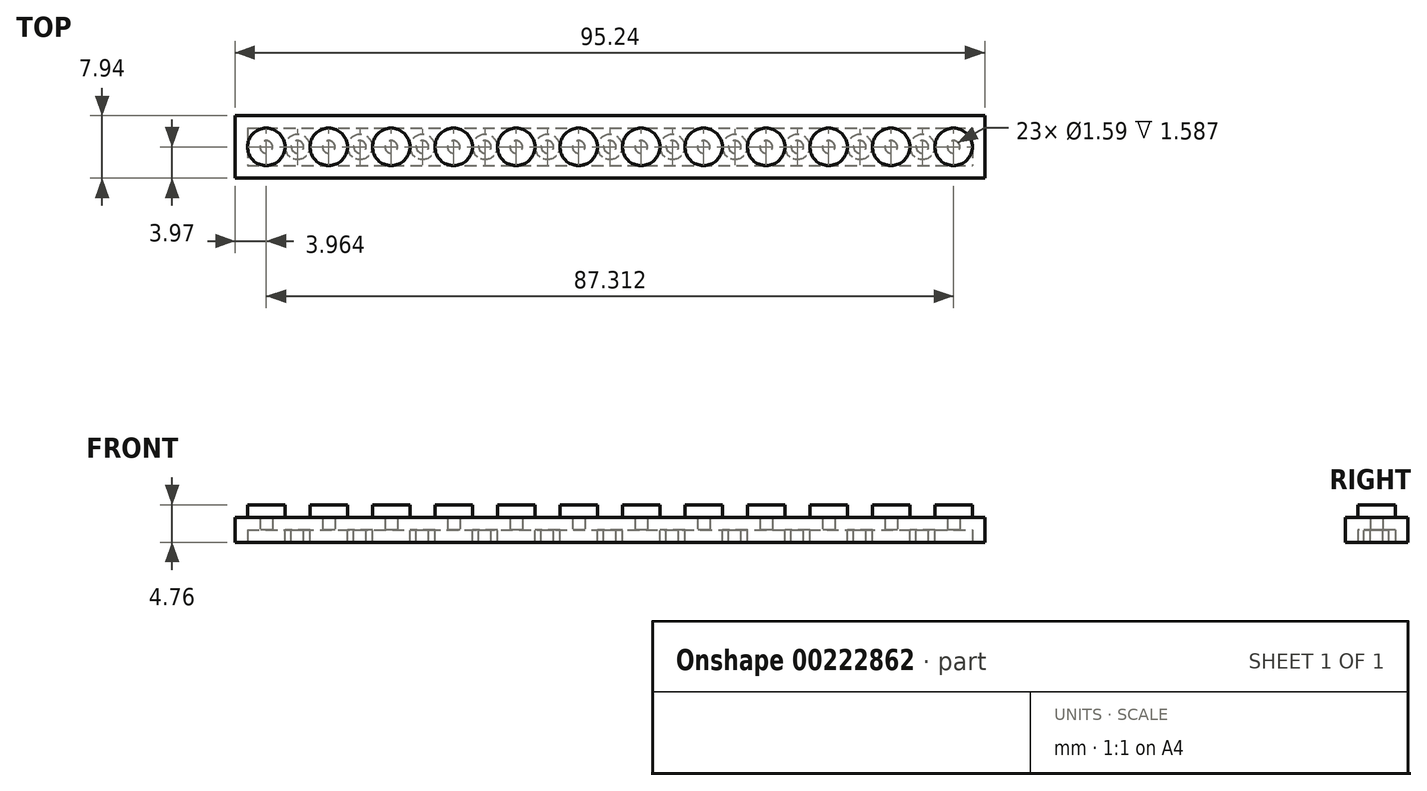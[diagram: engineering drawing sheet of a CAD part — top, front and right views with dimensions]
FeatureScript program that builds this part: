
annotation { "Feature Type Name" : "Feature", "Feature Type Description" : "" }
export const myFeature = defineFeature(function(context is Context, id is Id, definition is map)
    precondition{}
    {
        {
            var Q0;
            Q0=qCreatedBy(makeId("Top.planeOp"),FACE);
            var sketch = newSketch(context, id + "F0", { "sketchPlane" : qUnion([Q0])});
            skLineSegment(sketch, "E0.bottom", {"start": v(-47.63, 3.97) * mm, "end": v(47.62, 3.97) * mm});
            skLineSegment(sketch, "E0.top", {"start": v(-47.63, -3.97) * mm, "end": v(47.62, -3.97) * mm});
            skLineSegment(sketch, "E0.left", {"start": v(-47.63, 3.97) * mm, "end": v(-47.63, -3.97) * mm});
            skLineSegment(sketch, "E0.right", {"start": v(47.62, 3.97) * mm, "end": v(47.62, -3.97) * mm});
            skPoint(sketch, "E0.middle", {"position": v(0, 0) * mm});
            skCircle(sketch, "E1", {"center": v(-43.66, 0) * mm, "radius": 2.38 * mm});
            skCircle(sketch, "E2.1.0.0", {"center": v(-35.72, 0) * mm, "radius": 2.38 * mm});
            skCircle(sketch, "E2.2.0.0", {"center": v(-27.78, 0) * mm, "radius": 2.38 * mm});
            skLineSegment(sketch, "E2.direction1", {"start": v(-43.66, 0) * mm, "end": v(-35.72, 0) * mm, "construction": true});
            skCircle(sketch, "E3.0.3.0", {"center": v(-19.84, 0) * mm, "radius": 2.38 * mm});
            skCircle(sketch, "E4.0.4.0", {"center": v(-11.9, 0) * mm, "radius": 2.38 * mm});
            skCircle(sketch, "E4.0.5.0", {"center": v(-3.97, 0) * mm, "radius": 2.38 * mm});
            skCircle(sketch, "E4.0.6.0", {"center": v(3.97, 0) * mm, "radius": 2.38 * mm});
            skCircle(sketch, "E4.0.7.0", {"center": v(11.9, 0) * mm, "radius": 2.38 * mm});
            skCircle(sketch, "E5.0.8.0", {"center": v(19.84, 0) * mm, "radius": 2.38 * mm});
            skCircle(sketch, "E5.0.9.0", {"center": v(27.78, 0) * mm, "radius": 2.38 * mm});
            skCircle(sketch, "E5.0.10.0", {"center": v(35.72, 0) * mm, "radius": 2.38 * mm});
            skCircle(sketch, "E5.0.11.0", {"center": v(43.66, 0) * mm, "radius": 2.38 * mm});
            skSolve(sketch);
        }
        {
            var Q0;
            Q0=makeQuery(id+"F0.imprint","IMPRINT",FACE,{"disambiguationData":[TD([[makeQuery(id+"F0.imprint","IMPRINT",EDGE,{"derivedFrom":sQuery(id+"F0.wireOp",EDGE,"E0.bottom")}),-1.0]])]});
            extrude(context, id + "F1", {"entities" : qUnion([Q0]), "depth" : 3.17 * mm});
        }
        {
            var Q0;
            Q0=makeQuery(id+"F0.imprint","IMPRINT",FACE,{"disambiguationData":[TD([[makeQuery(id+"F0.imprint","IMPRINT",EDGE,{"derivedFrom":sQuery(id+"F0.wireOp",EDGE,"8b71ed98-f0e1-4300-85cb-82ad82c44b3e0.MirrorC")}),-1.0]])]});
            var Q1;
            Q1=makeQuery(id+"F0.imprint","IMPRINT",FACE,{"disambiguationData":[TD([[makeQuery(id+"F0.imprint","IMPRINT",EDGE,{"derivedFrom":sQuery(id+"F0.wireOp",EDGE,"E1")}),1.0]])]});
            var Q2;
            Q2=makeQuery(id+"F0.imprint","IMPRINT",FACE,{"disambiguationData":[TD([[makeQuery(id+"F0.imprint","IMPRINT",EDGE,{"derivedFrom":sQuery(id+"F0.wireOp",EDGE,"E2.2.0.0")}),1.0]])]});
            var Q3;
            Q3=makeQuery(id+"F0.imprint","IMPRINT",FACE,{"disambiguationData":[TD([[makeQuery(id+"F0.imprint","IMPRINT",EDGE,{"derivedFrom":sQuery(id+"F0.wireOp",EDGE,"E2.1.0.0")}),1.0]])]});
            var Q4;
            Q4=makeQuery(id+"F0.imprint","IMPRINT",FACE,{"disambiguationData":[TD([[makeQuery(id+"F0.imprint","IMPRINT",EDGE,{"derivedFrom":sQuery(id+"F0.wireOp",EDGE,"E3.0.3.0")}),1.0]])]});
            var Q5;
            Q5=makeQuery(id+"F0.imprint","IMPRINT",FACE,{"disambiguationData":[TD([[makeQuery(id+"F0.imprint","IMPRINT",EDGE,{"derivedFrom":sQuery(id+"F0.wireOp",EDGE,"E4.0.4.0")}),1.0]])]});
            var Q6;
            Q6=makeQuery(id+"F0.imprint","IMPRINT",FACE,{"disambiguationData":[TD([[makeQuery(id+"F0.imprint","IMPRINT",EDGE,{"derivedFrom":sQuery(id+"F0.wireOp",EDGE,"E4.0.5.0")}),1.0]])]});
            var Q7;
            Q7=makeQuery(id+"F0.imprint","IMPRINT",FACE,{"disambiguationData":[TD([[makeQuery(id+"F0.imprint","IMPRINT",EDGE,{"derivedFrom":sQuery(id+"F0.wireOp",EDGE,"E4.0.6.0")}),1.0]])]});
            var Q8;
            Q8=makeQuery(id+"F0.imprint","IMPRINT",FACE,{"disambiguationData":[TD([[makeQuery(id+"F0.imprint","IMPRINT",EDGE,{"derivedFrom":sQuery(id+"F0.wireOp",EDGE,"E4.0.7.0")}),1.0]])]});
            var Q9;
            Q9=makeQuery(id+"F0.imprint","IMPRINT",FACE,{"disambiguationData":[TD([[makeQuery(id+"F0.imprint","IMPRINT",EDGE,{"derivedFrom":sQuery(id+"F0.wireOp",EDGE,"E5.0.8.0")}),1.0]])]});
            var Q10;
            Q10=makeQuery(id+"F0.imprint","IMPRINT",FACE,{"disambiguationData":[TD([[makeQuery(id+"F0.imprint","IMPRINT",EDGE,{"derivedFrom":sQuery(id+"F0.wireOp",EDGE,"E5.0.9.0")}),1.0]])]});
            var Q11;
            Q11=makeQuery(id+"F0.imprint","IMPRINT",FACE,{"disambiguationData":[TD([[makeQuery(id+"F0.imprint","IMPRINT",EDGE,{"derivedFrom":sQuery(id+"F0.wireOp",EDGE,"E5.0.10.0")}),1.0]])]});
            var Q12;
            Q12=makeQuery(id+"F0.imprint","IMPRINT",FACE,{"disambiguationData":[TD([[makeQuery(id+"F0.imprint","IMPRINT",EDGE,{"derivedFrom":sQuery(id+"F0.wireOp",EDGE,"E5.0.11.0")}),1.0]])]});
            extrude(context, id + "F2", {"entities" : qUnion([Q0, Q1, Q2, Q3, Q4, Q5, Q6, Q7, Q8, Q9, Q10, Q11, Q12]), "operationType" : NewBodyOperationType.ADD, "depth" : 4.76 * mm});
        }
        {
            var Q0;
            {var subQ0=sQuery(id+"F0.wireOp",EDGE,"8b71ed98-f0e1-4300-85cb-82ad82c44b3e0.MirrorC");var subQ1=sQuery(id+"F0.wireOp",EDGE,"E1");Q0=makeQuery(id+"F2.boolean.opBoolean","MERGE",FACE,{"derivedFrom":[makeQuery(id+"F1.opExtrude","CAP_FACE",FACE,{"disambiguationData":[OSD([sQuery(id+"F0.wireOp",EDGE,"E0.bottom"),sQuery(id+"F0.wireOp",EDGE,"E0.top"),sQuery(id+"F0.wireOp",EDGE,"E0.left"),sQuery(id+"F0.wireOp",EDGE,"E0.right"),subQ1,subQ0])],"isStart":true}),makeQuery(id+"F2.opExtrude","CAP_FACE",FACE,{"disambiguationData":[OSD([subQ1])],"isStart":true}),makeQuery(id+"F2.opExtrude","CAP_FACE",FACE,{"disambiguationData":[OSD([subQ0])],"isStart":true})]});}
            shell(context, id + "F3", {"entities" : qUnion([Q0]), "thickness" : 1.59 * mm});
        }
        {
            var Q0;
            Q0=makeQuery(id+"F3.opShell","OFFSET_FACE",FACE,{"disambiguationData":[OSD([sQuery(id+"F0.wireOp",EDGE,"E0.bottom"),sQuery(id+"F0.wireOp",EDGE,"E0.top"),sQuery(id+"F0.wireOp",EDGE,"E0.left"),sQuery(id+"F0.wireOp",EDGE,"E0.right"),sQuery(id+"F0.wireOp",EDGE,"E1"),sQuery(id+"F0.wireOp",EDGE,"8b71ed98-f0e1-4300-85cb-82ad82c44b3e0.MirrorC")])]});
            var sketch = newSketch(context, id + "F4", { "sketchPlane" : qUnion([Q0])});
            skCircle(sketch, "E6.1.0.0", {"center": v(-39.69, 0) * mm, "radius": 1.59 * mm});
            skCircle(sketch, "E6.1.0.1", {"center": v(-39.69, 0) * mm, "radius": 0.8 * mm});
            skCircle(sketch, "E7.1.0.0", {"center": v(-31.75, 0) * mm, "radius": 1.59 * mm});
            skCircle(sketch, "E7.1.0.1", {"center": v(-31.75, 0) * mm, "radius": 0.8 * mm});
            skCircle(sketch, "E7.2.0.0", {"center": v(-23.81, 0) * mm, "radius": 1.59 * mm});
            skCircle(sketch, "E7.2.0.1", {"center": v(-23.81, 0) * mm, "radius": 0.8 * mm});
            skCircle(sketch, "E7.3.0.0", {"center": v(-15.88, 0) * mm, "radius": 1.59 * mm});
            skCircle(sketch, "E7.3.0.1", {"center": v(-15.88, 0) * mm, "radius": 0.8 * mm});
            skCircle(sketch, "E7.4.0.0", {"center": v(-7.94, 0) * mm, "radius": 1.59 * mm});
            skCircle(sketch, "E7.4.0.1", {"center": v(-7.94, 0) * mm, "radius": 0.8 * mm});
            skCircle(sketch, "E7.5.0.0", {"center": v(0, 0) * mm, "radius": 1.59 * mm});
            skCircle(sketch, "E7.5.0.1", {"center": v(0, 0) * mm, "radius": 0.8 * mm});
            skCircle(sketch, "E7.6.0.0", {"center": v(7.94, 0) * mm, "radius": 1.59 * mm});
            skCircle(sketch, "E7.6.0.1", {"center": v(7.94, 0) * mm, "radius": 0.8 * mm});
            skLineSegment(sketch, "E7.direction1", {"start": v(-39.69, 0) * mm, "end": v(-31.75, 0) * mm, "construction": true});
            skCircle(sketch, "E8.0.7.0", {"center": v(15.87, 0) * mm, "radius": 1.59 * mm});
            skCircle(sketch, "E8.2.7.0", {"center": v(15.87, 0) * mm, "radius": 0.8 * mm});
            skCircle(sketch, "E8.0.8.0", {"center": v(23.81, 0) * mm, "radius": 1.59 * mm});
            skCircle(sketch, "E8.2.8.0", {"center": v(23.81, 0) * mm, "radius": 0.8 * mm});
            skCircle(sketch, "E8.0.9.0", {"center": v(31.75, 0) * mm, "radius": 1.59 * mm});
            skCircle(sketch, "E8.2.9.0", {"center": v(31.75, 0) * mm, "radius": 0.8 * mm});
            skCircle(sketch, "E8.0.10.0", {"center": v(39.69, 0) * mm, "radius": 1.59 * mm});
            skCircle(sketch, "E8.2.10.0", {"center": v(39.69, 0) * mm, "radius": 0.8 * mm});
            skSolve(sketch);
        }
        {
            var Q0;
            Q0=makeQuery(id+"F4.imprint","IMPRINT",FACE,{"disambiguationData":[TD([[makeQuery(id+"F4.imprint","IMPRINT",EDGE,{"derivedFrom":sQuery(id+"F4.wireOp",EDGE,"E6.1.0.0")}),1.0]])]});
            var Q1;
            Q1=makeQuery(id+"F4.imprint","IMPRINT",FACE,{"disambiguationData":[TD([[makeQuery(id+"F4.imprint","IMPRINT",EDGE,{"derivedFrom":sQuery(id+"F4.wireOp",EDGE,"E7.1.0.0")}),1.0]])]});
            var Q2;
            Q2=makeQuery(id+"F4.imprint","IMPRINT",FACE,{"disambiguationData":[TD([[makeQuery(id+"F4.imprint","IMPRINT",EDGE,{"derivedFrom":sQuery(id+"F4.wireOp",EDGE,"E7.2.0.0")}),1.0]])]});
            var Q3;
            Q3=makeQuery(id+"F4.imprint","IMPRINT",FACE,{"disambiguationData":[TD([[makeQuery(id+"F4.imprint","IMPRINT",EDGE,{"derivedFrom":sQuery(id+"F4.wireOp",EDGE,"E7.3.0.0")}),1.0]])]});
            var Q4;
            Q4=makeQuery(id+"F4.imprint","IMPRINT",FACE,{"disambiguationData":[TD([[makeQuery(id+"F4.imprint","IMPRINT",EDGE,{"derivedFrom":sQuery(id+"F4.wireOp",EDGE,"E7.4.0.0")}),1.0]])]});
            var Q5;
            Q5=makeQuery(id+"F4.imprint","IMPRINT",FACE,{"disambiguationData":[TD([[makeQuery(id+"F4.imprint","IMPRINT",EDGE,{"derivedFrom":sQuery(id+"F4.wireOp",EDGE,"E7.5.0.0")}),1.0]])]});
            var Q6;
            Q6=makeQuery(id+"F4.imprint","IMPRINT",FACE,{"disambiguationData":[TD([[makeQuery(id+"F4.imprint","IMPRINT",EDGE,{"derivedFrom":sQuery(id+"F4.wireOp",EDGE,"E7.6.0.0")}),1.0]])]});
            var Q7;
            Q7=makeQuery(id+"F4.imprint","IMPRINT",FACE,{"disambiguationData":[TD([[makeQuery(id+"F4.imprint","IMPRINT",EDGE,{"derivedFrom":sQuery(id+"F4.wireOp",EDGE,"E8.0.7.0")}),1.0]])]});
            var Q8;
            Q8=makeQuery(id+"F4.imprint","IMPRINT",FACE,{"disambiguationData":[TD([[makeQuery(id+"F4.imprint","IMPRINT",EDGE,{"derivedFrom":sQuery(id+"F4.wireOp",EDGE,"E8.0.8.0")}),1.0]])]});
            var Q9;
            Q9=makeQuery(id+"F4.imprint","IMPRINT",FACE,{"disambiguationData":[TD([[makeQuery(id+"F4.imprint","IMPRINT",EDGE,{"derivedFrom":sQuery(id+"F4.wireOp",EDGE,"E8.0.9.0")}),1.0]])]});
            var Q10;
            Q10=makeQuery(id+"F4.imprint","IMPRINT",FACE,{"disambiguationData":[TD([[makeQuery(id+"F4.imprint","IMPRINT",EDGE,{"derivedFrom":sQuery(id+"F4.wireOp",EDGE,"E8.0.10.0")}),1.0]])]});
            extrude(context, id + "F5", {"entities" : qUnion([Q0, Q1, Q2, Q3, Q4, Q5, Q6, Q7, Q8, Q9, Q10]), "operationType" : NewBodyOperationType.ADD, "depth" : 1.59 * mm});
        }
    });
